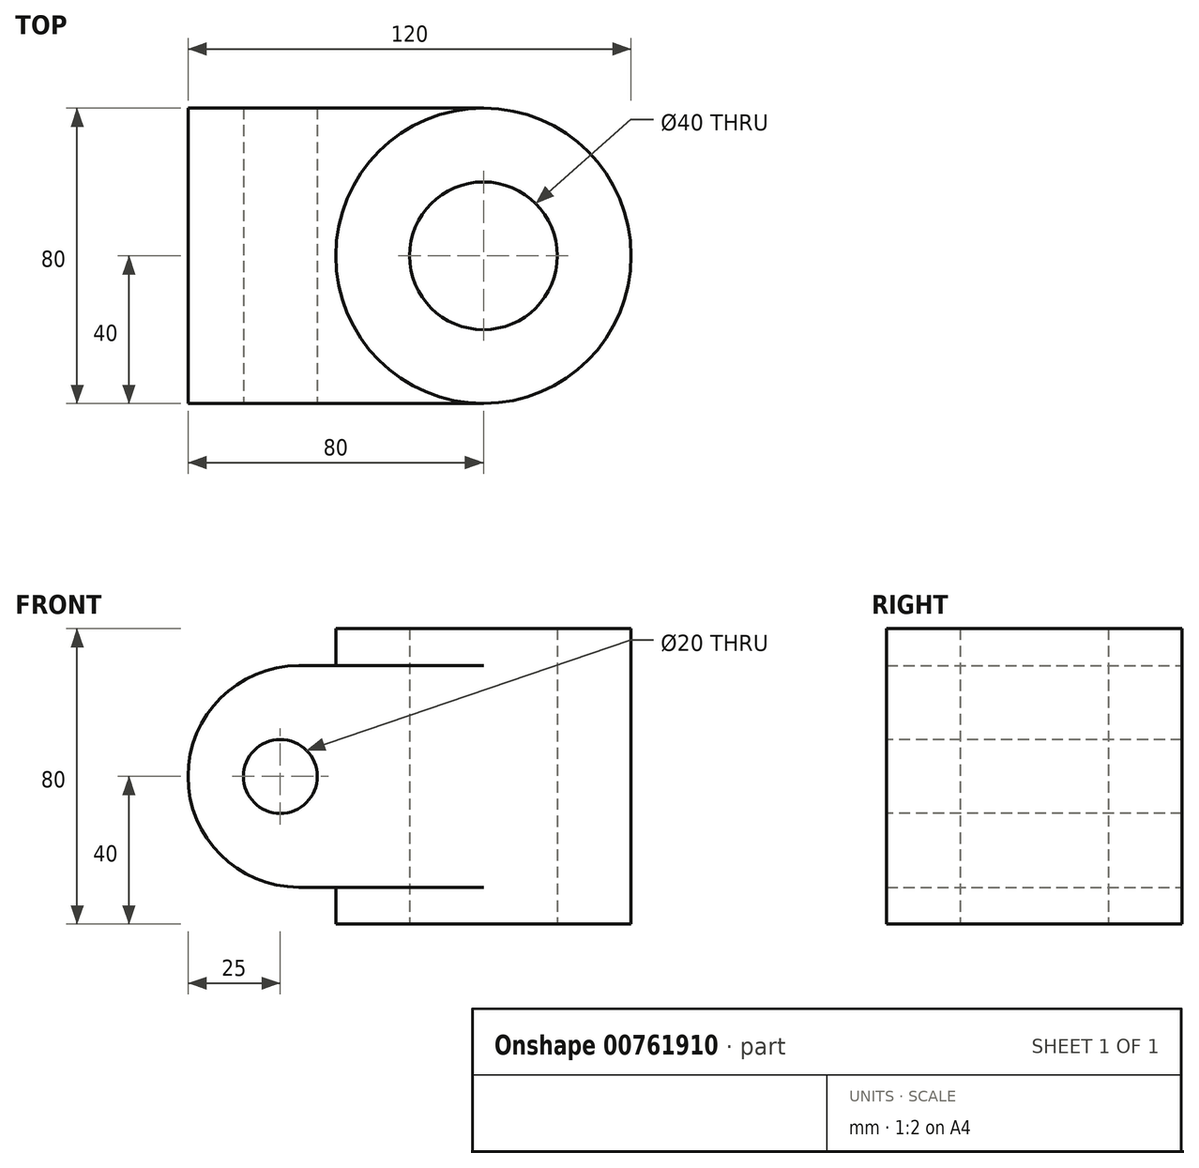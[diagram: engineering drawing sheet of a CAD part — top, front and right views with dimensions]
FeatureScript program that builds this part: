
annotation { "Feature Type Name" : "Feature", "Feature Type Description" : "" }
export const myFeature = defineFeature(function(context is Context, id is Id, definition is map)
    precondition{}
    {
        {
            var Q0;
            Q0=qCreatedBy(makeId("Top.planeOp"),FACE);
            var sketch = newSketch(context, id + "F0", { "sketchPlane" : qUnion([Q0])});
            skCircle(sketch, "E0", {"center": v(0, 0) * mm, "radius": 40 * mm});
            skCircle(sketch, "E1", {"center": v(0, 0) * mm, "radius": 20 * mm});
            skSolve(sketch);
        }
        {
            var Q0;
            Q0=makeQuery(id+"F0.imprint","IMPRINT",FACE,{"disambiguationData":[TD([[makeQuery(id+"F0.imprint","IMPRINT",EDGE,{"derivedFrom":sQuery(id+"F0.wireOp",EDGE,"E0")}),1.0]])]});
            extrude(context, id + "F1", {"entities" : qUnion([Q0]), "depth" : 80 * mm, "offsetDistance" : 25 * mm});
        }
        {
            var Q0;
            Q0=qCreatedBy(makeId("Front.planeOp"),FACE);
            var sketch = newSketch(context, id + "F2", { "sketchPlane" : qUnion([Q0])});
            skLineSegment(sketch, "E2.bottom", {"start": v(0, 10) * mm, "end": v(-80, 10) * mm});
            skLineSegment(sketch, "E2.top", {"start": v(0, 70) * mm, "end": v(-80, 70) * mm});
            skLineSegment(sketch, "E2.left", {"start": v(0, 10) * mm, "end": v(0, 70) * mm});
            skLineSegment(sketch, "E2.right", {"start": v(-80, 10) * mm, "end": v(-80, 70) * mm});
            skSolve(sketch);
        }
        {
            var Q0;
            Q0=makeQuery(id+"F2.imprint","IMPRINT",FACE,{"disambiguationData":[TD([[makeQuery(id+"F2.imprint","IMPRINT",EDGE,{"derivedFrom":sQuery(id+"F2.wireOp",EDGE,"E2.bottom")}),-1.0]])]});
            extrude(context, id + "F3", {"entities" : qUnion([Q0]), "operationType" : NewBodyOperationType.ADD, "endBound" : BoundingType.SYMMETRIC, "depth" : 80 * mm, "offsetDistance" : 25 * mm});
        }
        {
            var Q0;
            Q0=makeQuery(id+"F3.opExtrude","SWEPT_EDGE",EDGE,{"disambiguationData":[OSD([sQuery(id+"F2.wireOp",EDGE,"E2.top"),sQuery(id+"F2.wireOp",EDGE,"E2.right")])]});
            var Q1;
            Q1=makeQuery(id+"F3.opExtrude","SWEPT_EDGE",EDGE,{"disambiguationData":[OSD([sQuery(id+"F2.wireOp",EDGE,"E2.bottom"),sQuery(id+"F2.wireOp",EDGE,"E2.right")])]});
            fillet(context, id + "F4", {"entities" : qUnion([Q0, Q1]), "radius" : 30 * mm, "tangentPropagation" : true, "allowEdgeOverflow" : false});
        }
        {
            var Q0;
            Q0=makeQuery(id+"F3.boolean.opBoolean","SPLIT",FACE,{"disambiguationData":[TD([makeQuery(id+"F1.opExtrude","SWEPT_FACE",FACE,{"disambiguationData":[OSD([sQuery(id+"F0.wireOp",EDGE,"E1")])]})])],"derivedFrom":makeQuery(id+"F3.opExtrude","SWEPT_FACE",FACE,{"disambiguationData":[OSD([sQuery(id+"F2.wireOp",EDGE,"E2.top")])]})});
            extrude(context, id + "F5", {"entities" : qUnion([Q0]), "operationType" : NewBodyOperationType.REMOVE, "endBound" : BoundingType.THROUGH_ALL, "oppositeDirection" : true, "depth" : 25 * mm, "offsetDistance" : 25 * mm});
        }
        {
            var Q0;
            Q0=makeQuery(id+"F3.opExtrude","CAP_FACE",FACE,{"disambiguationData":[OSD([sQuery(id+"F2.wireOp",EDGE,"E2.bottom"),sQuery(id+"F2.wireOp",EDGE,"E2.top"),sQuery(id+"F2.wireOp",EDGE,"E2.left"),sQuery(id+"F2.wireOp",EDGE,"E2.right")])],"isStart":false});
            var sketch = newSketch(context, id + "F6", { "sketchPlane" : qUnion([Q0])});
            skCircle(sketch, "E3", {"center": v(-55, 40) * mm, "radius": 10 * mm});
            skSolve(sketch);
        }
        {
            var Q0;
            Q0=makeQuery(id+"F6.imprint","IMPRINT",FACE,{"disambiguationData":[TD([[makeQuery(id+"F6.imprint","IMPRINT",EDGE,{"derivedFrom":sQuery(id+"F6.wireOp",EDGE,"E3")}),1.0]])]});
            extrude(context, id + "F7", {"entities" : qUnion([Q0]), "operationType" : NewBodyOperationType.REMOVE, "endBound" : BoundingType.THROUGH_ALL, "oppositeDirection" : true, "depth" : 25 * mm, "offsetDistance" : 25 * mm});
        }
    });
